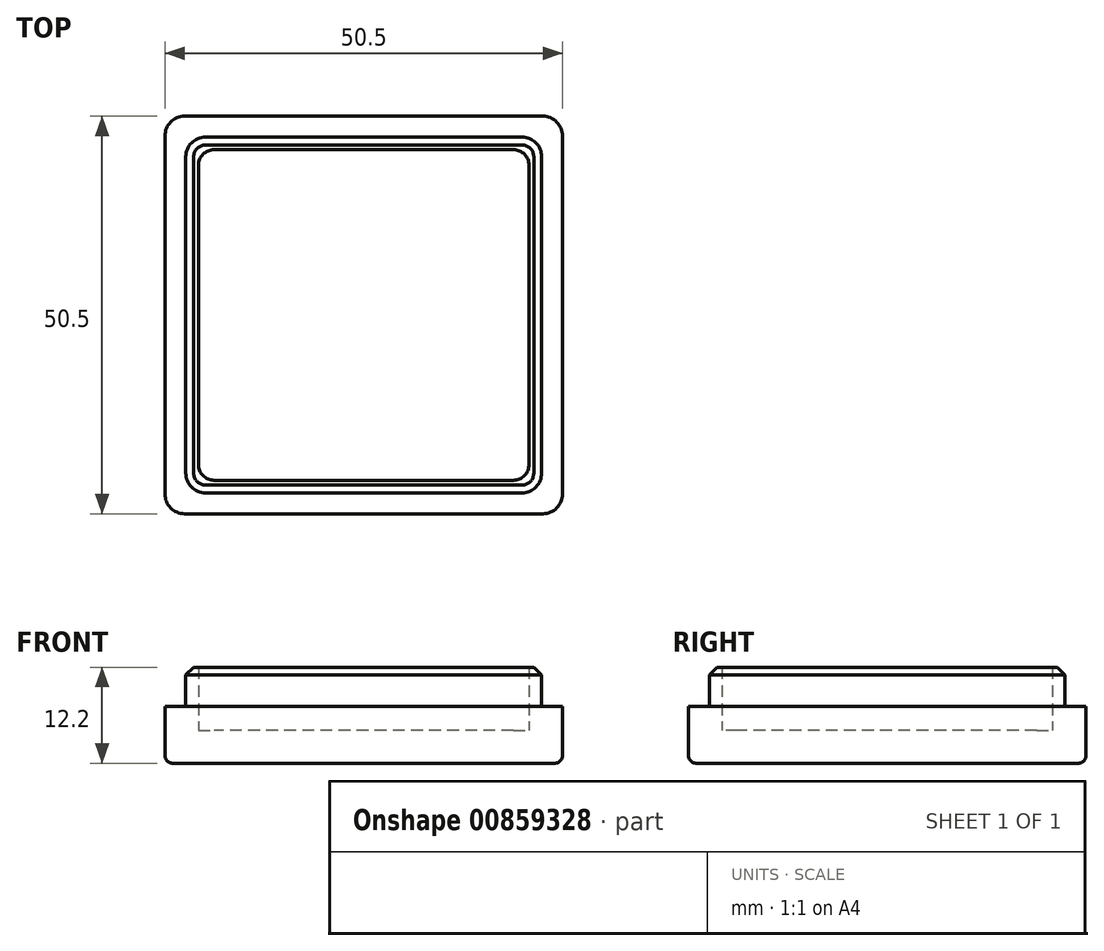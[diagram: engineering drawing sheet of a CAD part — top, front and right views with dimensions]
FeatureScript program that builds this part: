
annotation { "Feature Type Name" : "Feature", "Feature Type Description" : "" }
export const myFeature = defineFeature(function(context is Context, id is Id, definition is map)
    precondition{}
    {
        {
            var Q0;
            Q0=qCreatedBy(makeId("Top.planeOp"),FACE);
            var sketch = newSketch(context, id + "F0", { "sketchPlane" : qUnion([Q0])});
            skLineSegment(sketch, "E0.bottom", {"start": v(25.25, 25.25) * mm, "end": v(-25.25, 25.25) * mm});
            skLineSegment(sketch, "E0.top", {"start": v(25.25, -25.25) * mm, "end": v(-25.25, -25.25) * mm});
            skLineSegment(sketch, "E0.left", {"start": v(25.25, 25.25) * mm, "end": v(25.25, -25.25) * mm});
            skLineSegment(sketch, "E0.right", {"start": v(-25.25, 25.25) * mm, "end": v(-25.25, -25.25) * mm});
            skPoint(sketch, "E0.middle", {"position": v(0, 0) * mm});
            skSolve(sketch);
        }
        {
            var Q0;
            Q0=qSketchRegion(id+"F0",true);
            extrude(context, id + "F1", {"entities" : qUnion([Q0]), "depth" : (2 + 5.2) * mm, "offsetDistance" : 25 * mm});
        }
        {
            var Q0;
            Q0=makeQuery(id+"F1.opExtrude","CAP_FACE",FACE,{"disambiguationData":[OSD([sQuery(id+"F0.wireOp",EDGE,"E0.bottom"),sQuery(id+"F0.wireOp",EDGE,"E0.top"),sQuery(id+"F0.wireOp",EDGE,"E0.left"),sQuery(id+"F0.wireOp",EDGE,"E0.right")])],"isStart":false});
            var sketch = newSketch(context, id + "F2", { "sketchPlane" : qUnion([Q0])});
            skLineSegment(sketch, "E1.bottom", {"start": v(22.6, 22.6) * mm, "end": v(-22.6, 22.6) * mm});
            skLineSegment(sketch, "E1.top", {"start": v(22.6, -22.6) * mm, "end": v(-22.6, -22.6) * mm});
            skLineSegment(sketch, "E1.left", {"start": v(22.6, 22.6) * mm, "end": v(22.6, -22.6) * mm});
            skLineSegment(sketch, "E1.right", {"start": v(-22.6, 22.6) * mm, "end": v(-22.6, -22.6) * mm});
            skPoint(sketch, "E1.middle", {"position": v(0, 0) * mm});
            skSolve(sketch);
        }
        {
            var Q0;
            Q0=qSketchRegion(id+"F2",true);
            extrude(context, id + "F3", {"entities" : qUnion([Q0]), "operationType" : NewBodyOperationType.ADD, "depth" : 5 * mm, "offsetDistance" : 25 * mm});
        }
        {
            var Q0;
            Q0=makeQuery(id+"F1.opExtrude","CAP_FACE",FACE,{"disambiguationData":[OSD([sQuery(id+"F0.wireOp",EDGE,"E0.bottom"),sQuery(id+"F0.wireOp",EDGE,"E0.top"),sQuery(id+"F0.wireOp",EDGE,"E0.left"),sQuery(id+"F0.wireOp",EDGE,"E0.right")])],"isStart":false});
            var sketch = newSketch(context, id + "F4", { "sketchPlane" : qUnion([Q0])});
            skLineSegment(sketch, "E2.bottom", {"start": v(21, 21) * mm, "end": v(-21, 21) * mm});
            skLineSegment(sketch, "E2.top", {"start": v(21, -21) * mm, "end": v(-21, -21) * mm});
            skLineSegment(sketch, "E2.left", {"start": v(21, 21) * mm, "end": v(21, -21) * mm});
            skLineSegment(sketch, "E2.right", {"start": v(-21, 21) * mm, "end": v(-21, -21) * mm});
            skPoint(sketch, "E2.middle", {"position": v(0, 0) * mm});
            skSolve(sketch);
        }
        {
            var Q0;
            Q0=qSketchRegion(id+"F4",true);
            extrude(context, id + "F5", {"entities" : qUnion([Q0]), "operationType" : NewBodyOperationType.REMOVE, "endBound" : BoundingType.UP_TO_NEXT, "depth" : 25 * mm, "offsetDistance" : 25 * mm, "hasSecondDirection" : true, "secondDirectionOppositeDirection" : true, "secondDirectionDepth" : 3 * mm});
        }
        {
            var Q0;
            Q0=makeQuery(id+"F1.opExtrude","SWEPT_EDGE",EDGE,{"disambiguationData":[OSD([sQuery(id+"F0.wireOp",EDGE,"E0.bottom"),sQuery(id+"F0.wireOp",EDGE,"E0.right")])]});
            var Q1;
            Q1=makeQuery(id+"F1.opExtrude","SWEPT_EDGE",EDGE,{"disambiguationData":[OSD([sQuery(id+"F0.wireOp",EDGE,"E0.top"),sQuery(id+"F0.wireOp",EDGE,"E0.right")])]});
            var Q2;
            Q2=makeQuery(id+"F1.opExtrude","SWEPT_EDGE",EDGE,{"disambiguationData":[OSD([sQuery(id+"F0.wireOp",EDGE,"E0.top"),sQuery(id+"F0.wireOp",EDGE,"E0.left")])]});
            var Q3;
            Q3=makeQuery(id+"F1.opExtrude","SWEPT_EDGE",EDGE,{"disambiguationData":[OSD([sQuery(id+"F0.wireOp",EDGE,"E0.bottom"),sQuery(id+"F0.wireOp",EDGE,"E0.left")])]});
            var Q4;
            Q4=makeQuery(id+"F3.opExtrude","SWEPT_EDGE",EDGE,{"disambiguationData":[OSD([sQuery(id+"F2.wireOp",EDGE,"E1.bottom"),sQuery(id+"F2.wireOp",EDGE,"E1.right")])]});
            var Q5;
            Q5=makeQuery(id+"F3.opExtrude","SWEPT_EDGE",EDGE,{"disambiguationData":[OSD([sQuery(id+"F2.wireOp",EDGE,"E1.top"),sQuery(id+"F2.wireOp",EDGE,"E1.right")])]});
            var Q6;
            Q6=makeQuery(id+"F3.opExtrude","SWEPT_EDGE",EDGE,{"disambiguationData":[OSD([sQuery(id+"F2.wireOp",EDGE,"E1.top"),sQuery(id+"F2.wireOp",EDGE,"E1.left")])]});
            var Q7;
            Q7=makeQuery(id+"F3.opExtrude","SWEPT_EDGE",EDGE,{"disambiguationData":[OSD([sQuery(id+"F2.wireOp",EDGE,"E1.bottom"),sQuery(id+"F2.wireOp",EDGE,"E1.left")])]});
            fillet(context, id + "F6", {"entities" : qUnion([Q0, Q1, Q2, Q3, Q4, Q5, Q6, Q7]), "radius" : 2.5 * mm, "tangentPropagation" : true, "allowEdgeOverflow" : false});
        }
        {
            var Q0;
            Q0=makeQuery(id+"F5.boolean.opBoolean","COPY",EDGE,{"derivedFrom":makeQuery(id+"F5.opExtrude","SWEPT_EDGE",EDGE,{"disambiguationData":[OSD([sQuery(id+"F4.wireOp",EDGE,"E2.bottom"),sQuery(id+"F4.wireOp",EDGE,"E2.right")])]})});
            var Q1;
            Q1=makeQuery(id+"F5.boolean.opBoolean","COPY",EDGE,{"derivedFrom":makeQuery(id+"F5.opExtrude","SWEPT_EDGE",EDGE,{"disambiguationData":[OSD([sQuery(id+"F4.wireOp",EDGE,"E2.bottom"),sQuery(id+"F4.wireOp",EDGE,"E2.left")])]})});
            var Q2;
            Q2=makeQuery(id+"F5.boolean.opBoolean","COPY",EDGE,{"derivedFrom":makeQuery(id+"F5.opExtrude","SWEPT_EDGE",EDGE,{"disambiguationData":[OSD([sQuery(id+"F4.wireOp",EDGE,"E2.top"),sQuery(id+"F4.wireOp",EDGE,"E2.left")])]})});
            var Q3;
            Q3=makeQuery(id+"F5.boolean.opBoolean","COPY",EDGE,{"derivedFrom":makeQuery(id+"F5.opExtrude","SWEPT_EDGE",EDGE,{"disambiguationData":[OSD([sQuery(id+"F4.wireOp",EDGE,"E2.top"),sQuery(id+"F4.wireOp",EDGE,"E2.right")])]})});
            fillet(context, id + "F7", {"entities" : qUnion([Q0, Q1, Q2, Q3]), "radius" : 2 * mm, "tangentPropagation" : true, "allowEdgeOverflow" : false});
        }
        {
            var Q0;
            Q0=makeQuery(id+"F3.opExtrude","CAP_EDGE",EDGE,{"disambiguationData":[OSD([sQuery(id+"F2.wireOp",EDGE,"E1.right")])],"isStart":false});
            chamfer(context, id + "F8", {"entities" : qUnion([Q0]), "width" : 1 * mm, "tangentPropagation" : true});
        }
        {
            var Q0;
            Q0=makeQuery(id+"F1.opExtrude","CAP_EDGE",EDGE,{"disambiguationData":[OSD([sQuery(id+"F0.wireOp",EDGE,"E0.bottom")])],"isStart":true});
            fillet(context, id + "F9", {"entities" : qUnion([Q0]), "radius" : 1 * mm, "tangentPropagation" : true, "allowEdgeOverflow" : false});
        }
    });
